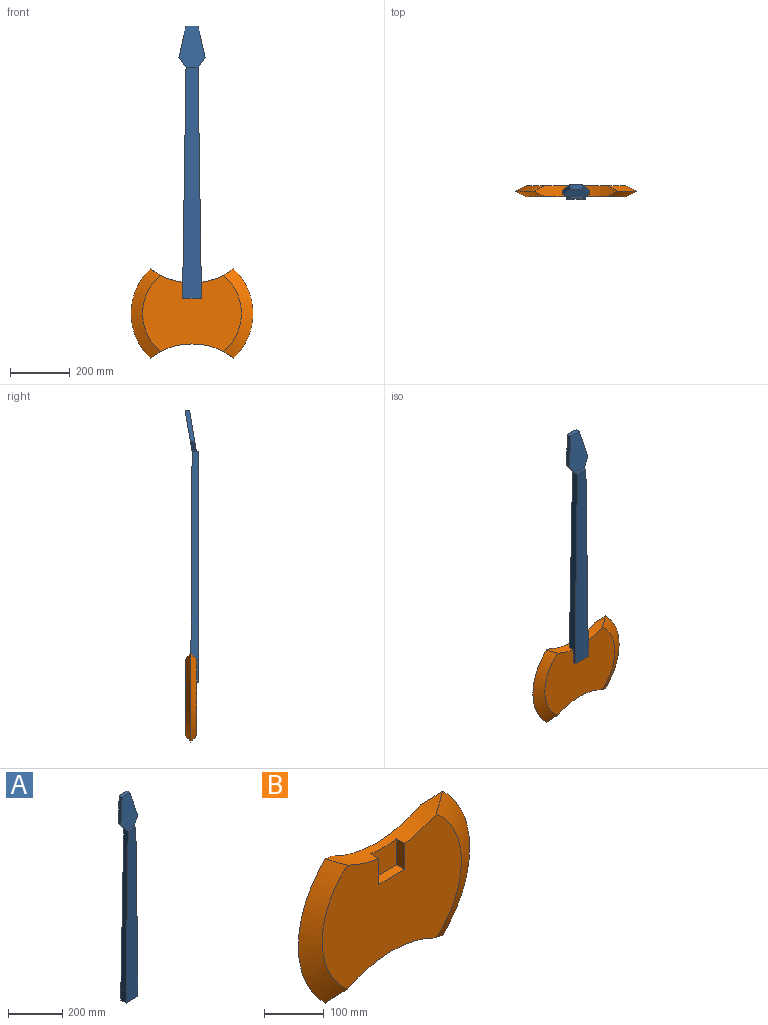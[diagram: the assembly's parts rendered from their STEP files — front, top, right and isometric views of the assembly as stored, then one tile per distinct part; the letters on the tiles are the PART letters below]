
ASSEMBLY  parts=2 mates=1
PART A: 17 faces, bbox 87.7x46.3x908.3 mm
  f0: plane 717.8x27.03mm, normal (-1,0,0.02), area 17905.3mm2, adj f1,f5,f7,f8,f14,f15
  f1: plane 50.8x27.03mm, normal (-1,0,0), area 1372.9mm2, adj f0,f2,f5,f6
  f2: plane 61.74x27.03mm, normal (0,0,-1), area 1668.5mm2, adj f1,f3,f5,f6
  f3: plane 50.8x27.03mm, normal (1,0,0), area 1372.9mm2, adj f2,f4,f5,f6
  f4: plane 717.8x27.03mm, normal (1,0,0.02), area 17905.3mm2, adj f3,f5,f7,f9,f14,f15
  f5: plane 768.57x61.74mm, normal (0,-1,0), area 39649mm2, adj f0,f1,f2,f3,f4,f14
  f6: plane 61.74x50.8mm, normal (0,1,0), area 3136.3mm2, adj f1,f2,f3,f7
  f7: plane 717.8x61.74mm, normal (0,1,0.01), area 36514.2mm2, adj f0,f4,f6,f15
  f8: plane 34x23.86mm, normal (-0.82,0,-0.57), area 605.4mm2, adj f0,f12,f15,f16
  f9: plane 34x23.86mm, normal (0.82,0,-0.57), area 605.4mm2, adj f4,f10,f15,f16
  f10: plane 105.7x32.35mm, normal (0.98,0,0.22), area 1602.5mm2, adj f9,f11,f13,f15,f16
  f11: plane 40x14.87mm, normal (0,0,1), area 594.7mm2, adj f10,f12,f13,f16
  f12: plane 105.7x32.35mm, normal (-0.98,0,0.22), area 1602.5mm2, adj f8,f11,f13,f15,f16
  f13: plane 40.22x0.49mm, normal (0,1,0), area 19.6mm2, adj f10,f11,f12,f15
  f14: plane 40x8.33mm, normal (0,0,1), area 333.3mm2, adj f0,f4,f5,f16
  f15: plane 139.21x87.73mm, normal (0,0.99,-0.17), area 9026.5mm2, adj f0,f4,f7,f8,f9,f10,f12,f13
  f16: plane 139.7x87.73mm, normal (0,-0.99,0.16), area 9042.9mm2, adj f8,f9,f10,f11,f12,f14
PART B: 12 faces, bbox 406.4x37.1x313.2 mm
  f0: cylinder r=228.6mm len=277.42mm, axis (0,1,0), area 8414.4mm2, adj f2,f3,f4,f5,f6,f7,f9,f10
  f1: cylinder r=228.6mm len=277.42mm, axis (0,1,0), area 9591.3mm2, adj f2,f3,f4,f5,f6,f7
  f2: plane 330.2x254.49mm, normal (0,-1,0), area 64289.1mm2, adj f0,f1,f4,f6,f8,f9,f10
  f3: plane 330.2x254.49mm, normal (0,1,0), area 67464.9mm2, adj f0,f1,f5,f7
  f4: cone r=165.1mm half-angle=64.1deg, axis (0,1,0), area 13157.5mm2, adj f0,f1,f2,f5
  f5: cone r=203.2mm half-angle=64.1deg, axis (0,-1,0), area 13157.5mm2, adj f0,f1,f3,f4
  f6: cone r=165.1mm half-angle=64.1deg, axis (0,1,0), area 13157.5mm2, adj f0,f1,f2,f7
  f7: cone r=203.2mm half-angle=64.1deg, axis (0,-1,0), area 13157.5mm2, adj f0,f1,f3,f6
  f8: plane 61.67x19.02mm, normal (0,0,1), area 1173.3mm2, adj f2,f9,f10,f11
  f9: plane 52.89x19.02mm, normal (-1,0,0), area 1006.2mm2, adj f0,f2,f8,f11
  f10: plane 52.89x19.02mm, normal (1,0,0), area 1006.2mm2, adj f0,f2,f8,f11
  f11: plane 61.67x52.89mm, normal (0,-1,0), area 3175.8mm2, adj f0,f8,f9,f10
PLACE A t=(-125.89,152.13,472.89)mm
PLACE B t=(-152.7,170.17,34.36)mm
MATE fastened B.f11 <-> A.f6  axis (0,-1,0) through (-178.72,152.13,87.4)mm
